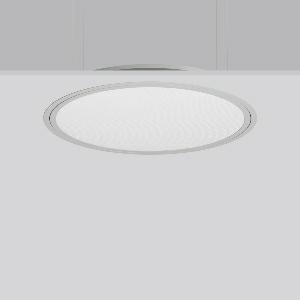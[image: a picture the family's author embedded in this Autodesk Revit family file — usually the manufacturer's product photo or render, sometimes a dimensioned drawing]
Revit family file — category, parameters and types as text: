
# Revit family: triona_round_e_312296_004_12_7214
name_source: partatom
category: Lighting Fixtures
units: mm (PartAtom-declared; Revit-internal decimal feet)

## family parameters
Cut with Voids When Loaded = No
Host = Face
Light Source = No
Part Type = Normal
Room Calculation Point = No
Round Connector Dimension = Use Diameter
Shared = No

## types (1)
- TRIONA round E (1 x LED Modul 830, 3750 lm, 3000)
    Apparent Load = 31 VA
    CIE Flux Codes = 58 86 97 100 100
    Color Rendering = 80
    Color Temperature = 3000
    Default Elevation = 1800 mm
    Description = Series: TRIONA round
Decorative round LED recessed surface luminaire. Cover made of sheet steel, powder-coated. Frame made of aluminium, powder-coated. Recessed ring: aluminium extrusion profile, powder coated. Light emission through a diffuser in plastic, opal/prismatic. Lightguide and diffuser made of non-yellowing plastic (PMMA). Lateral light emission (RZB SIDELITE technology) for above-average homogeneous light distribution. Suitable for installation in cavity ceilings. Tool-free mounting system thanks to the rocker arm mechanism (patent pending). Electronic ballast included. Very easy installation thanks to Plug+Play connection. Perfect for office areas (RUG < 19) and environments with computer screens in accordance with EN 12464-1. 
Colour: silver, matt (approx. RAL 9006)
Diameter: 725 mm
Height: 2 mm
Cut-out diameter: 702 mm
Recess height: 100 mm
Luminaire: recess height: 89 mm
Lamp: LED
Socket: without socket
Colour temperature: 3000K
Colour rendering index (CRI): 80
System power: 31 W
Rated luminous flux: 3750 lm
Luminous efficiency: 121 lm/W
Control gear: Converter, dimmable, DALI
Protection class: I
Type of protection: IP 40
    Height = 0 mm  [stored 0 ft]
    Lamp = 1 x LED Modul 830
    Lamp Light Flux = 3750 lm
    Lamp count = 1
    Length = 725 mm
    Lifetime = 50000 h
    Luminous efficacy = 121 lm/W
    Manufacturer = RZB
    ModVariant = No
    Model = 312296.004.12
    Mounting Place = Ceiling
    Mounting Type = Recessed
    Number of Poles = 1
    OnlyDefault = Yes
    Power Factor = 1
    Product Name = TRIONA round E
    Product group = Recessed modular luminaires
    ProductGroupID = 406
    Protection Class = Protection class I
    Protection Degree = IP 20
    RLX_Detail_Level = 1
    RLX_Emergency_Light_Flux = 0 lm
    RLX_Emergency_Type = 0
    RLX_Emergency_Type_DB = No
    RlxData = <blob elided: 37549 chars, md5=676b463a>
    Socket = socket
    Standby Power = 0 W
    System Light Flux = 3750 lm
    System Power = 31 W
    Type Comments = Product without accessories
    Type Image = 312296.004.12.jpg
    URL = http://relux.com
    VarID = ---
    Voltage = 230 V
    Voltage Range = 220-240 V
    Weight = 0.00 kg
    Width = 0 mm  [stored 0 ft]

note: [stored X ft] marks values corroborated as IEEE doubles in the binary element streams (Revit-internal decimal feet)

## geometry (parser evidence)
native form markers: Blend x4, Sweep x9
no freeform markers — native parametric forms only
